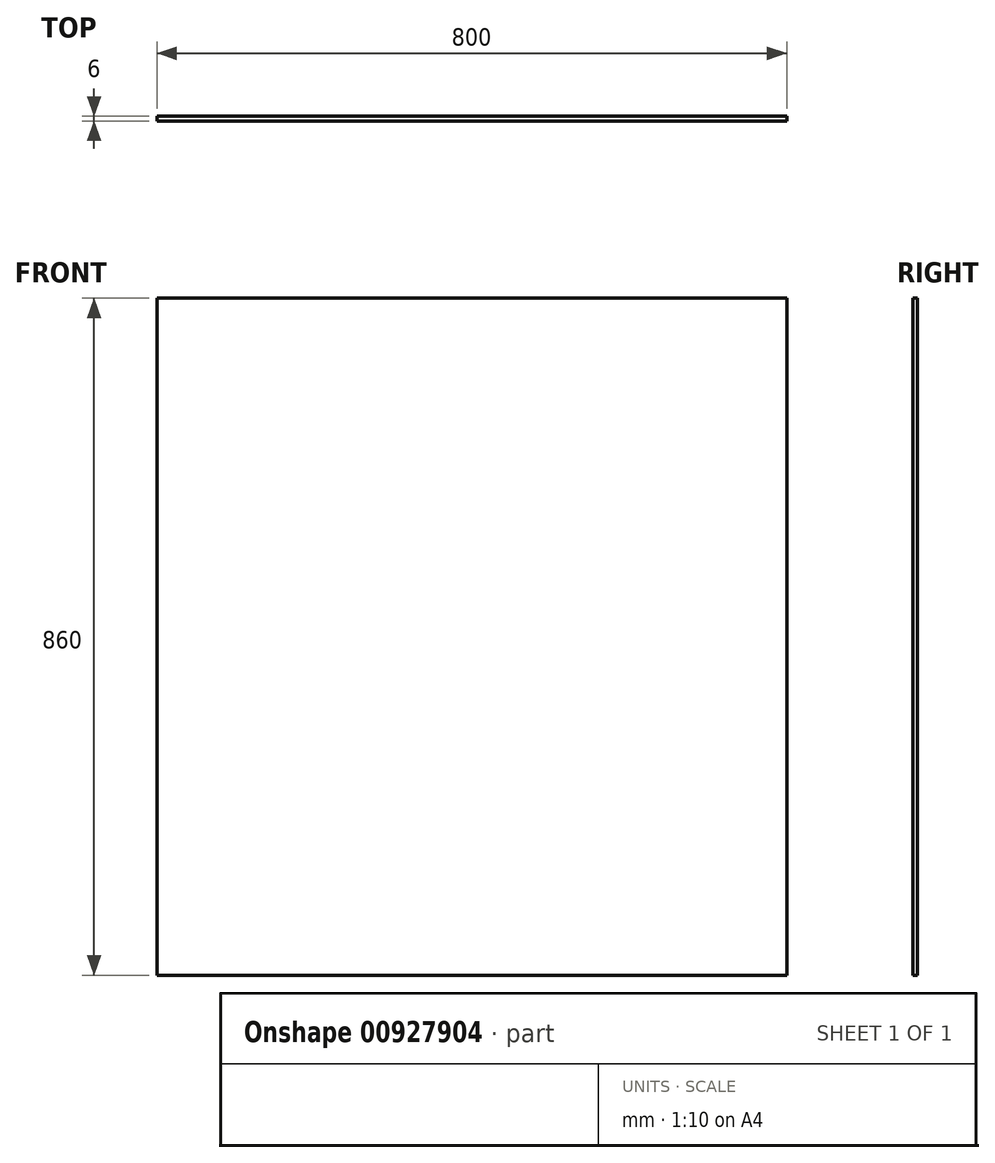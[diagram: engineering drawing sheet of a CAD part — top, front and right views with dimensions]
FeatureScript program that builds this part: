
annotation { "Feature Type Name" : "Feature", "Feature Type Description" : "" }
export const myFeature = defineFeature(function(context is Context, id is Id, definition is map)
    precondition{}
    {
        {
            var Q0;
            Q0=qCreatedBy(makeId("Front.planeOp"),FACE);
            var sketch = newSketch(context, id + "F0", { "sketchPlane" : qUnion([Q0])});
            skLineSegment(sketch, "E0.bottom", {"start": v(0, 0) * mm, "end": v(800, 0) * mm});
            skLineSegment(sketch, "E0.top", {"start": v(0, 860) * mm, "end": v(800, 860) * mm});
            skLineSegment(sketch, "E0.left", {"start": v(0, 0) * mm, "end": v(0, 860) * mm});
            skLineSegment(sketch, "E0.right", {"start": v(800, 0) * mm, "end": v(800, 860) * mm});
            skSolve(sketch);
        }
        {
            var Q0;
            Q0 = qSketchRegion(id + "F0", true);
            extrude(context, id + "F1", {"entities" : qUnion([Q0]), "depth" : 6 * mm, "offsetDistance" : 25 * mm});
        }
    });
